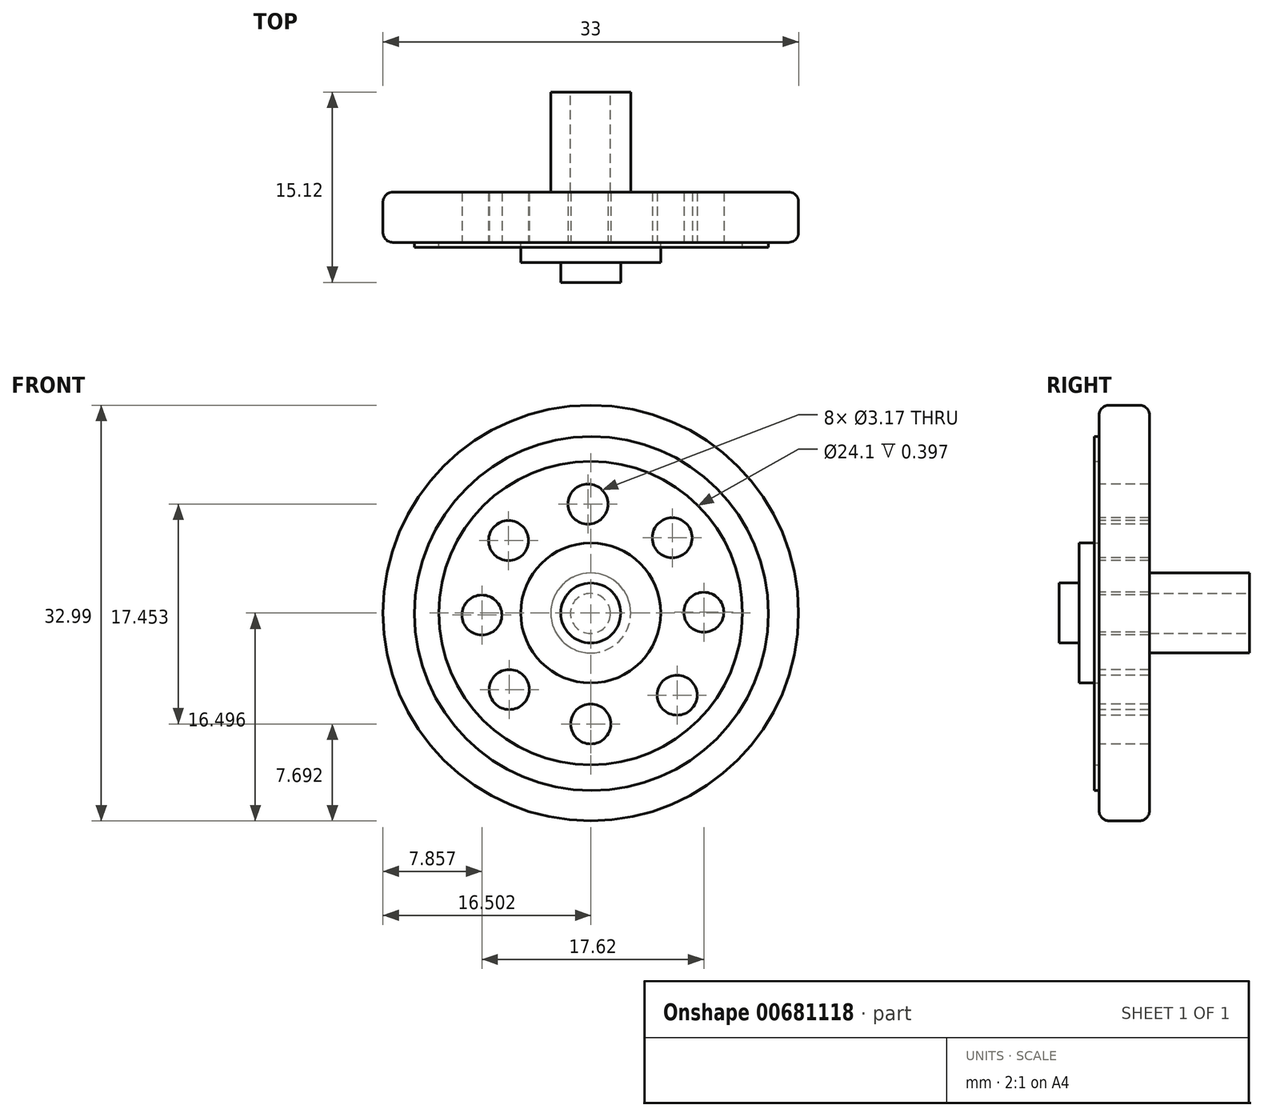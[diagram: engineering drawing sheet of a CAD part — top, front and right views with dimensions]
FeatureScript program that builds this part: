
annotation { "Feature Type Name" : "Feature", "Feature Type Description" : "" }
export const myFeature = defineFeature(function(context is Context, id is Id, definition is map)
    precondition{}
    {
        {
            var Q0;
            Q0=qCreatedBy(makeId("Front.planeOp"),FACE);
            var sketch = newSketch(context, id + "F0", { "sketchPlane" : qUnion([Q0])});
            skCircle(sketch, "E0", {"center": v(-21.24, 19.9) * mm, "radius": 16.5 * mm});
            skSolve(sketch);
        }
        {
            var Q0;
            Q0 = qSketchRegion(id + "F0", true);
            extrude(context, id + "F1", {"entities" : qUnion([Q0]), "oppositeDirection" : true, "depth" : 4 * mm, "offsetDistance" : 25.4 * mm});
        }
        {
            var Q0;
            Q0=makeQuery(id+"F1.opExtrude","CAP_EDGE",EDGE,{"disambiguationData":[OSD([sQuery(id+"F0.wireOp",EDGE,"E0")])],"isStart":true});
            var Q1;
            Q1=makeQuery(id+"F1.opExtrude","CAP_EDGE",EDGE,{"disambiguationData":[OSD([sQuery(id+"F0.wireOp",EDGE,"E0")])],"isStart":false});
            fillet(context, id + "F2", {"entities" : qUnion([Q0, Q1]), "radius" : 0.8 * mm, "tangentPropagation" : true, "allowEdgeOverflow" : false});
        }
        {
            var Q0;
            Q0=makeQuery(id+"F1.opExtrude","CAP_FACE",FACE,{"disambiguationData":[OSD([sQuery(id+"F0.wireOp",EDGE,"E0")])],"isStart":true});
            var sketch = newSketch(context, id + "F3", { "sketchPlane" : qUnion([Q0])});
            skCircle(sketch, "E1", {"center": v(-21.46, 28.54) * mm, "radius": 1.59 * mm});
            skSolve(sketch);
        }
        {
            var Q0;
            Q0 = qSketchRegion(id + "F3", true);
            extrude(context, id + "F4", {"entities" : qUnion([Q0]), "operationType" : NewBodyOperationType.REMOVE, "oppositeDirection" : true, "depth" : 13.2 * mm, "offsetDistance" : 25.4 * mm});
        }
        {
            var Q0;
            Q0=makeQuery(id+"F1.opExtrude","CAP_FACE",FACE,{"disambiguationData":[OSD([sQuery(id+"F0.wireOp",EDGE,"E0")])],"isStart":true});
            var sketch = newSketch(context, id + "F5", { "sketchPlane" : qUnion([Q0])});
            skCircle(sketch, "E2", {"center": v(-21.24, 11.1) * mm, "radius": 1.59 * mm});
            skSolve(sketch);
        }
        {
            var Q0;
            Q0 = qSketchRegion(id + "F5", true);
            extrude(context, id + "F6", {"entities" : qUnion([Q0]), "operationType" : NewBodyOperationType.REMOVE, "oppositeDirection" : true, "depth" : 12.7 * mm, "offsetDistance" : 25.4 * mm});
        }
        {
            var Q0;
            Q0=makeQuery(id+"F1.opExtrude","CAP_FACE",FACE,{"disambiguationData":[OSD([sQuery(id+"F0.wireOp",EDGE,"E0")])],"isStart":true});
            var sketch = newSketch(context, id + "F7", { "sketchPlane" : qUnion([Q0])});
            skCircle(sketch, "E3", {"center": v(-29.88, 19.73) * mm, "radius": 1.59 * mm});
            skSolve(sketch);
        }
        {
            var Q0;
            Q0 = qSketchRegion(id + "F7", true);
            extrude(context, id + "F8", {"entities" : qUnion([Q0]), "operationType" : NewBodyOperationType.REMOVE, "oppositeDirection" : true, "depth" : 25.4 * mm, "offsetDistance" : 25.4 * mm});
        }
        {
            var Q0;
            Q0=makeQuery(id+"F1.opExtrude","CAP_FACE",FACE,{"disambiguationData":[OSD([sQuery(id+"F0.wireOp",EDGE,"E0")])],"isStart":true});
            var sketch = newSketch(context, id + "F9", { "sketchPlane" : qUnion([Q0])});
            skCircle(sketch, "E4", {"center": v(-12.26, 19.96) * mm, "radius": 1.59 * mm});
            skSolve(sketch);
        }
        {
            var Q0;
            Q0 = qSketchRegion(id + "F9", true);
            extrude(context, id + "F10", {"entities" : qUnion([Q0]), "operationType" : NewBodyOperationType.REMOVE, "oppositeDirection" : true, "depth" : 25.4 * mm, "offsetDistance" : 25.4 * mm});
        }
        {
            var Q0;
            Q0=makeQuery(id+"F1.opExtrude","CAP_FACE",FACE,{"disambiguationData":[OSD([sQuery(id+"F0.wireOp",EDGE,"E0")])],"isStart":true});
            var sketch = newSketch(context, id + "F11", { "sketchPlane" : qUnion([Q0])});
            skCircle(sketch, "E5", {"center": v(-27.76, 25.65) * mm, "radius": 1.59 * mm});
            skSolve(sketch);
        }
        {
            var Q0;
            Q0 = qSketchRegion(id + "F11", true);
            extrude(context, id + "F12", {"entities" : qUnion([Q0]), "operationType" : NewBodyOperationType.REMOVE, "oppositeDirection" : true, "depth" : 25.4 * mm, "offsetDistance" : 25.4 * mm});
        }
        {
            var Q0;
            Q0=makeQuery(id+"F1.opExtrude","CAP_FACE",FACE,{"disambiguationData":[OSD([sQuery(id+"F0.wireOp",EDGE,"E0")])],"isStart":true});
            var sketch = newSketch(context, id + "F13", { "sketchPlane" : qUnion([Q0])});
            skCircle(sketch, "E6", {"center": v(-14.77, 25.87) * mm, "radius": 1.59 * mm});
            skSolve(sketch);
        }
        {
            var Q0;
            Q0 = qSketchRegion(id + "F13", true);
            extrude(context, id + "F14", {"entities" : qUnion([Q0]), "operationType" : NewBodyOperationType.REMOVE, "oppositeDirection" : true, "depth" : 25.4 * mm, "offsetDistance" : 25.4 * mm});
        }
        {
            var Q0;
            Q0=makeQuery(id+"F1.opExtrude","CAP_FACE",FACE,{"disambiguationData":[OSD([sQuery(id+"F0.wireOp",EDGE,"E0")])],"isStart":true});
            var sketch = newSketch(context, id + "F15", { "sketchPlane" : qUnion([Q0])});
            skCircle(sketch, "E7", {"center": v(-27.7, 13.82) * mm, "radius": 1.59 * mm});
            skSolve(sketch);
        }
        {
            var Q0;
            Q0 = qSketchRegion(id + "F15", true);
            extrude(context, id + "F16", {"entities" : qUnion([Q0]), "operationType" : NewBodyOperationType.REMOVE, "oppositeDirection" : true, "depth" : 25.4 * mm, "offsetDistance" : 25.4 * mm});
        }
        {
            var Q0;
            Q0=makeQuery(id+"F1.opExtrude","CAP_FACE",FACE,{"disambiguationData":[OSD([sQuery(id+"F0.wireOp",EDGE,"E0")])],"isStart":true});
            var sketch = newSketch(context, id + "F17", { "sketchPlane" : qUnion([Q0])});
            skCircle(sketch, "E8", {"center": v(-14.38, 13.38) * mm, "radius": 1.59 * mm});
            skSolve(sketch);
        }
        {
            var Q0;
            Q0 = qSketchRegion(id + "F17", true);
            extrude(context, id + "F18", {"entities" : qUnion([Q0]), "operationType" : NewBodyOperationType.REMOVE, "oppositeDirection" : true, "depth" : 25.4 * mm, "offsetDistance" : 25.4 * mm});
        }
        {
            var Q0;
            Q0=makeQuery(id+"F1.opExtrude","CAP_FACE",FACE,{"disambiguationData":[OSD([sQuery(id+"F0.wireOp",EDGE,"E0")])],"isStart":true});
            var sketch = newSketch(context, id + "F19", { "sketchPlane" : qUnion([Q0])});
            skCircle(sketch, "E9", {"center": v(-21.24, 19.9) * mm, "radius": 5.56 * mm});
            skSolve(sketch);
        }
        {
            var Q0;
            Q0 = qSketchRegion(id + "F19", true);
            extrude(context, id + "F20", {"entities" : qUnion([Q0]), "operationType" : NewBodyOperationType.ADD, "depth" : 1.59 * mm, "offsetDistance" : 25.4 * mm});
        }
        {
            var Q0;
            Q0=makeQuery(id+"F20.opExtrude","CAP_FACE",FACE,{"disambiguationData":[OSD([sQuery(id+"F19.wireOp",EDGE,"E9")])],"isStart":false});
            var sketch = newSketch(context, id + "F21", { "sketchPlane" : qUnion([Q0])});
            skCircle(sketch, "E10", {"center": v(-21.24, 19.9) * mm, "radius": 2.38 * mm});
            skSolve(sketch);
        }
        {
            var Q0;
            Q0 = qSketchRegion(id + "F21", true);
            extrude(context, id + "F22", {"entities" : qUnion([Q0]), "operationType" : NewBodyOperationType.ADD, "depth" : 1.59 * mm, "offsetDistance" : 25.4 * mm});
        }
        {
            var Q0;
            Q0=makeQuery(id+"F1.opExtrude","CAP_FACE",FACE,{"disambiguationData":[OSD([sQuery(id+"F0.wireOp",EDGE,"E0")])],"isStart":true});
            var sketch = newSketch(context, id + "F23", { "sketchPlane" : qUnion([Q0])});
            skCircle(sketch, "E11", {"center": v(-21.24, 19.9) * mm, "radius": 12.05 * mm});
            skSolve(sketch);
        }
        {
            var Q0;
            Q0=makeQuery(id+"F23.imprint","IMPRINT",FACE,{"disambiguationData":[TD([[makeQuery(id+"F23.imprint","IMPRINT",EDGE,{"derivedFrom":sQuery(id+"F23.wireOp",EDGE,"E11")}),-1.0]])]});
            var sketch = newSketch(context, id + "F24", { "sketchPlane" : qUnion([Q0])});
            skCircle(sketch, "E12", {"center": v(-21.18, 19.86) * mm, "radius": 14.05 * mm});
            skSolve(sketch);
        }
        {
            var Q0;
            Q0=makeQuery(id+"F24.imprint","IMPRINT",FACE,{"disambiguationData":[TD([[makeQuery(id+"F24.imprint","IMPRINT",EDGE,{"derivedFrom":sQuery(id+"F24.wireOp",EDGE,"E12")}),1.0]])]});
            extrude(context, id + "F25", {"entities" : qUnion([Q0]), "operationType" : NewBodyOperationType.ADD, "depth" : 0.4 * mm, "offsetDistance" : 25.4 * mm});
        }
        {
            var Q0;
            Q0=makeQuery(id+"F1.opExtrude","CAP_FACE",FACE,{"disambiguationData":[OSD([sQuery(id+"F0.wireOp",EDGE,"E0")])],"isStart":false});
            var sketch = newSketch(context, id + "F26", { "sketchPlane" : qUnion([Q0])});
            skCircle(sketch, "E13", {"center": v(21.24, 19.9) * mm, "radius": 3.18 * mm});
            skSolve(sketch);
        }
        {
            var Q0;
            Q0 = qSketchRegion(id + "F26", true);
            extrude(context, id + "F27", {"entities" : qUnion([Q0]), "operationType" : NewBodyOperationType.ADD, "depth" : 7.94 * mm, "offsetDistance" : 25.4 * mm});
        }
        {
            var Q0;
            Q0=makeQuery(id+"F27.opExtrude","CAP_FACE",FACE,{"disambiguationData":[OSD([sQuery(id+"F26.wireOp",EDGE,"E13")])],"isStart":false});
            var sketch = newSketch(context, id + "F28", { "sketchPlane" : qUnion([Q0])});
            skSolve(sketch);
        }
        {
            var Q0;
            Q0=makeQuery(id+"F28.imprint","IMPRINT",FACE,{"disambiguationData":[TD([[makeQuery(id+"F28.imprint","IMPRINT",EDGE,{"derivedFrom":makeQuery(id+"F27.opExtrude","CAP_EDGE",EDGE,{"disambiguationData":[OSD([sQuery(id+"F26.wireOp",EDGE,"E13")])],"isStart":false})}),1.0]])]});
            var sketch = newSketch(context, id + "F29", { "sketchPlane" : qUnion([Q0])});
            skCircle(sketch, "E14", {"center": v(21.26, 19.87) * mm, "radius": 1.59 * mm});
            skSolve(sketch);
        }
        {
            var Q0;
            Q0 = qSketchRegion(id + "F29", true);
            extrude(context, id + "F30", {"entities" : qUnion([Q0]), "operationType" : NewBodyOperationType.REMOVE, "oppositeDirection" : true, "depth" : 7.94 * mm, "offsetDistance" : 25.4 * mm});
        }
    });
